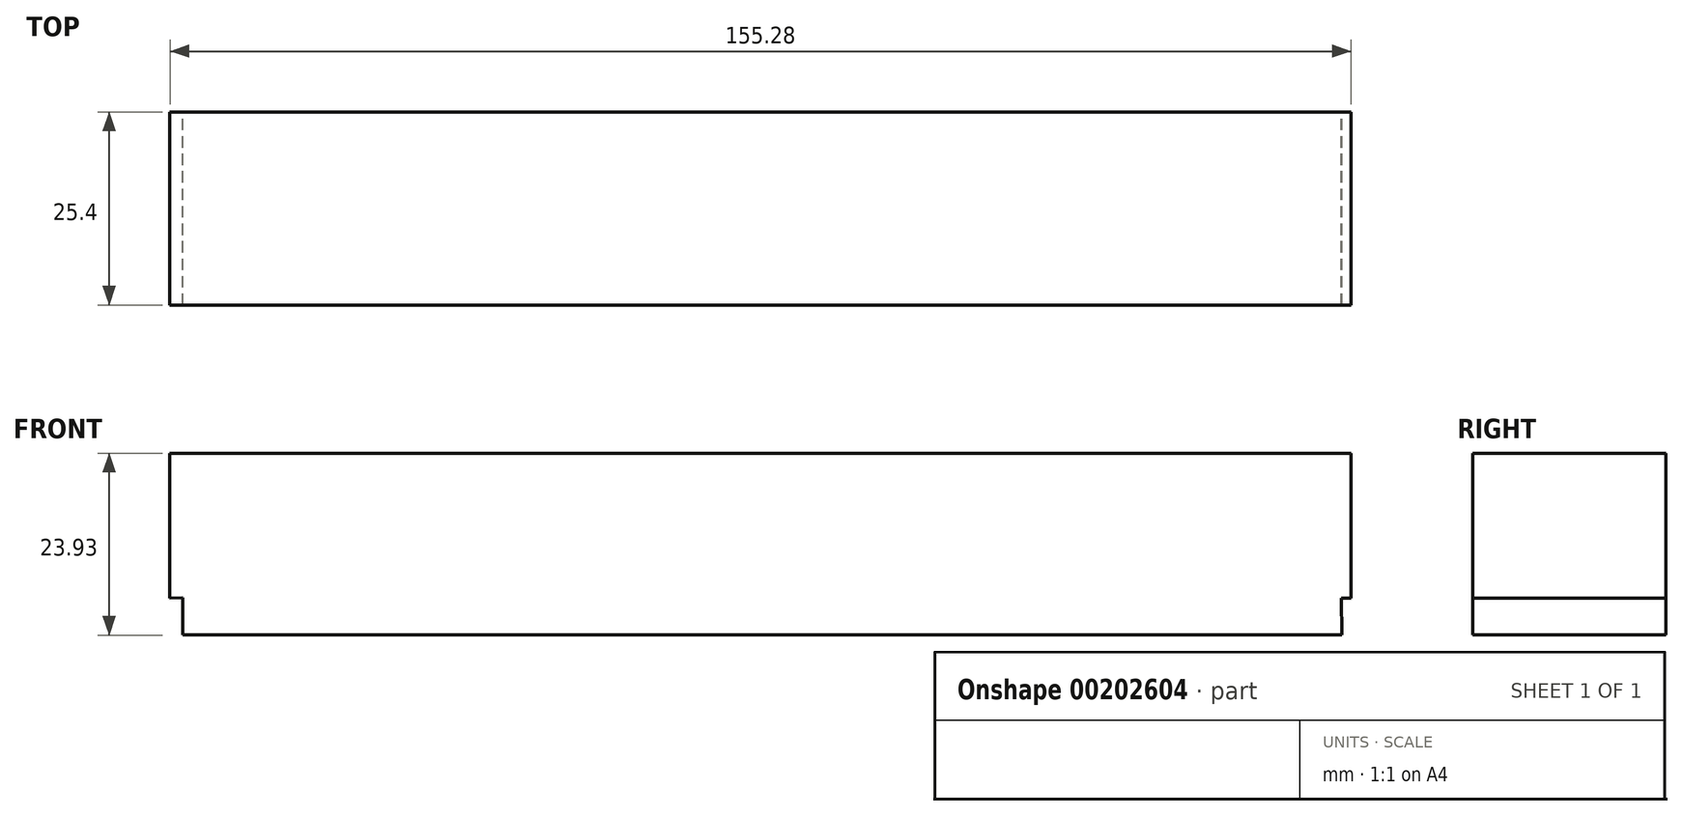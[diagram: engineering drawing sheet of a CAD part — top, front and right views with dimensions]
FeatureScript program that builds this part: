
annotation { "Feature Type Name" : "Feature", "Feature Type Description" : "" }
export const myFeature = defineFeature(function(context is Context, id is Id, definition is map)
    precondition{}
    {
        {
            var Q0;
            Q0=qCreatedBy(makeId("Front.planeOp"),FACE);
            var sketch = newSketch(context, id + "F0", { "sketchPlane" : qUnion([Q0])});
            skLineSegment(sketch, "E0", {"start": v(-80.3, -23.85) * mm, "end": v(-80.3, -4.8) * mm});
            skLineSegment(sketch, "E1", {"start": v(-80.3, -4.8) * mm, "end": v(74.98, -4.8) * mm});
            skLineSegment(sketch, "E2", {"start": v(74.98, -4.8) * mm, "end": v(74.98, -23.85) * mm});
            skLineSegment(sketch, "E3", {"start": v(73.7, -23.87) * mm, "end": v(74.98, -23.85) * mm});
            skLineSegment(sketch, "E4", {"start": v(73.8, -28.73) * mm, "end": v(73.7, -23.87) * mm});
            skLineSegment(sketch, "E5", {"start": v(73.8, -28.73) * mm, "end": v(-78.6, -28.73) * mm});
            skLineSegment(sketch, "E6", {"start": v(-78.6, -23.8) * mm, "end": v(-78.6, -28.73) * mm});
            skPoint(sketch, "E7.end.orphan", {"position": v(-77.06, -23.8) * mm});
            skLineSegment(sketch, "E8", {"start": v(-80.3, -23.85) * mm, "end": v(-78.6, -23.8) * mm});
            skSolve(sketch);
        }
        {
            var Q0;
            Q0 = qSketchRegion(id + "F0", true);
            extrude(context, id + "F1", {"entities" : qUnion([Q0]), "depth" : 25.4 * mm});
        }
    });
